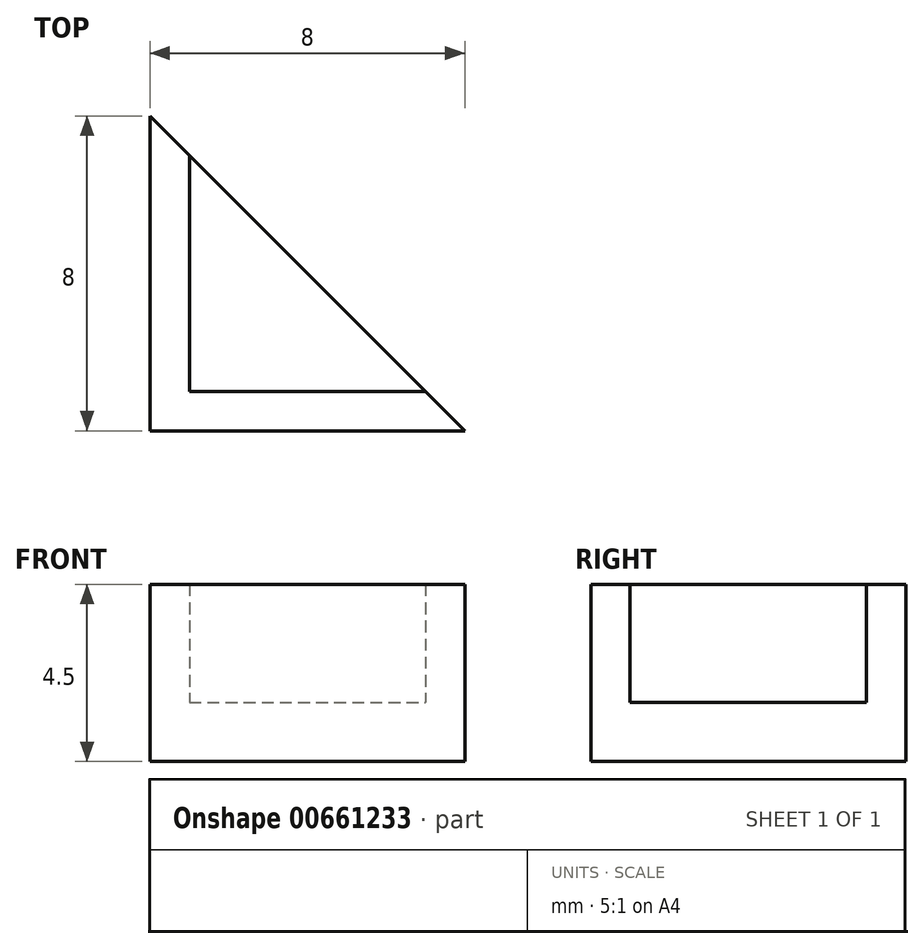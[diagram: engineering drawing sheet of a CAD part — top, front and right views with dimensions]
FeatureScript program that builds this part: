
annotation { "Feature Type Name" : "Feature", "Feature Type Description" : "" }
export const myFeature = defineFeature(function(context is Context, id is Id, definition is map)
    precondition{}
    {
        {
            var Q0;
            Q0=qCreatedBy(makeId("Top.planeOp"),FACE);
            var sketch = newSketch(context, id + "F0", { "sketchPlane" : qUnion([Q0])});
            skLineSegment(sketch, "E0", {"start": v(0, 0) * mm, "end": v(0, 8) * mm});
            skLineSegment(sketch, "E1", {"start": v(0, 8) * mm, "end": v(8, 0) * mm});
            skLineSegment(sketch, "E2", {"start": v(8, 0) * mm, "end": v(0, 0) * mm});
            skSolve(sketch);
        }
        {
            var Q0;
            Q0=makeQuery(id+"F0.imprint","IMPRINT",FACE,{"disambiguationData":[TD([[makeQuery(id+"F0.imprint","IMPRINT",EDGE,{"derivedFrom":sQuery(id+"F0.wireOp",EDGE,"E0")}),-1.0]])]});
            extrude(context, id + "F1", {"entities" : qUnion([Q0]), "depth" : 1.5 * mm, "offsetDistance" : 25 * mm});
        }
        {
            var Q0;
            Q0=makeQuery(id+"F1.opExtrude","CAP_FACE",FACE,{"disambiguationData":[OSD([sQuery(id+"F0.wireOp",EDGE,"E0"),sQuery(id+"F0.wireOp",EDGE,"E1"),sQuery(id+"F0.wireOp",EDGE,"E2")])],"isStart":false});
            var sketch = newSketch(context, id + "F2", { "sketchPlane" : qUnion([Q0])});
            skLineSegment(sketch, "E3", {"start": v(1, 7) * mm, "end": v(1, 1) * mm});
            skLineSegment(sketch, "E4", {"start": v(1, 1) * mm, "end": v(7, 1) * mm});
            skLineSegment(sketch, "E5", {"start": v(7, 1) * mm, "end": v(8, 0) * mm});
            skLineSegment(sketch, "E6", {"start": v(8, 0) * mm, "end": v(0, 0) * mm});
            skLineSegment(sketch, "E7", {"start": v(0, 0) * mm, "end": v(0, 8) * mm});
            skLineSegment(sketch, "E8", {"start": v(0, 8) * mm, "end": v(1, 7) * mm});
            skSolve(sketch);
        }
        {
            var Q0;
            Q0=makeQuery(id+"F2.imprint","IMPRINT",FACE,{"disambiguationData":[TD([[makeQuery(id+"F2.imprint","IMPRINT",EDGE,{"derivedFrom":sQuery(id+"F2.wireOp",EDGE,"E3")}),-1.0]])]});
            extrude(context, id + "F3", {"entities" : qUnion([Q0]), "operationType" : NewBodyOperationType.ADD, "depth" : 3 * mm, "offsetDistance" : 25 * mm});
        }
    });
